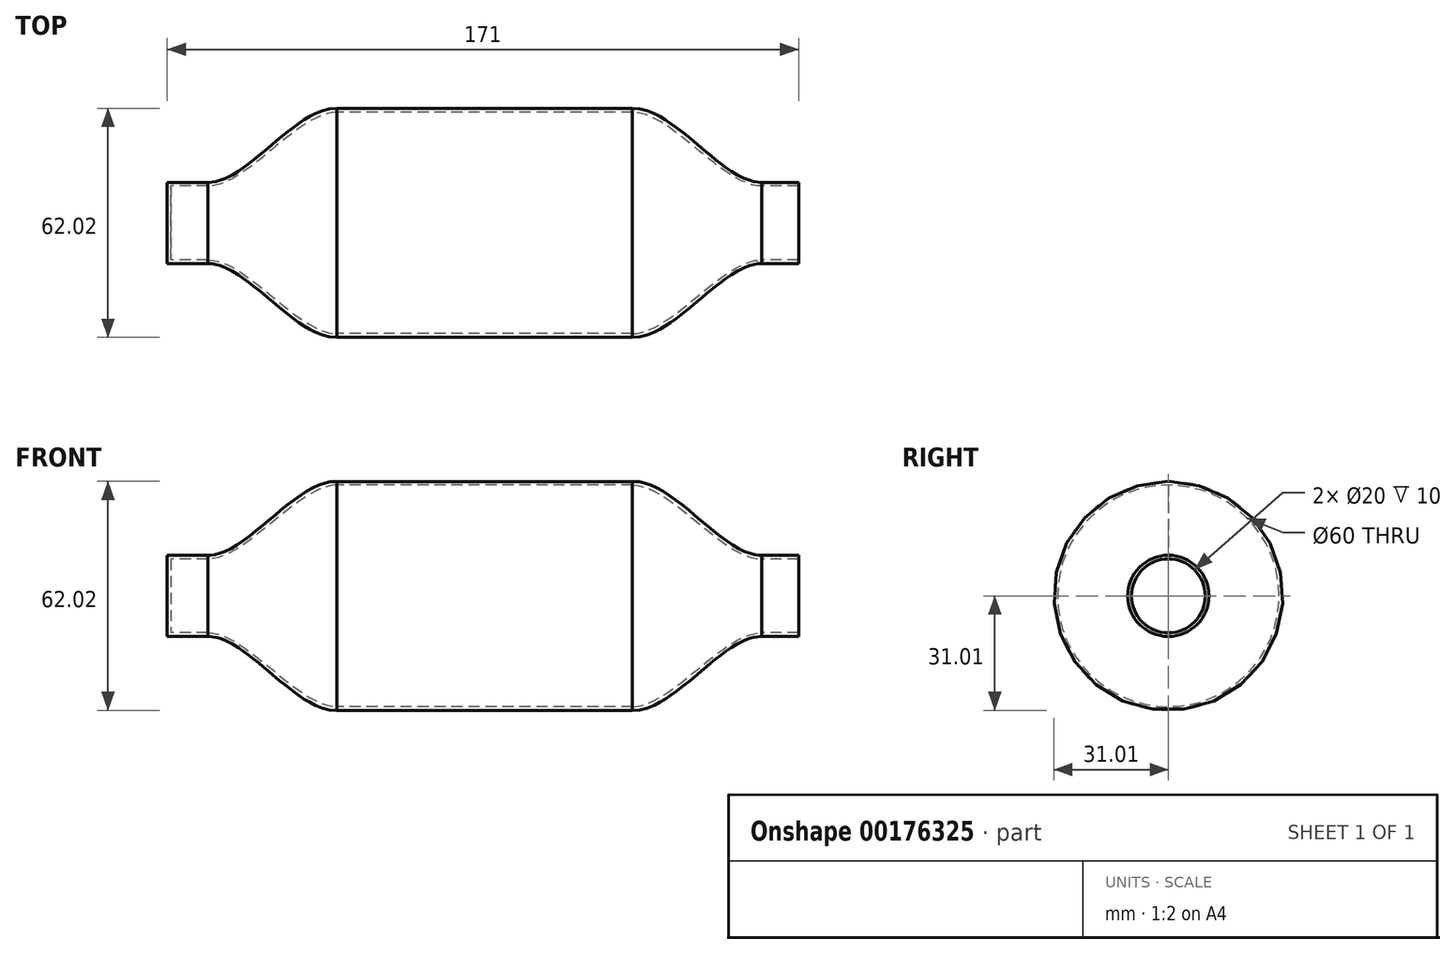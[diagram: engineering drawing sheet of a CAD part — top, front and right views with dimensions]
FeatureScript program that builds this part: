
annotation { "Feature Type Name" : "Feature", "Feature Type Description" : "" }
export const myFeature = defineFeature(function(context is Context, id is Id, definition is map)
    precondition{}
    {
        {
            var Q0;
            Q0=qCreatedBy(makeId("Top.planeOp"),FACE);
            var sketch = newSketch(context, id + "F0", { "sketchPlane" : qUnion([Q0])});
            skLineSegment(sketch, "E0", {"start": v(-46.54, 10) * mm, "end": v(-36.54, 10) * mm});
            skLineSegment(sketch, "E1", {"start": v(123.46, 10) * mm, "end": v(113.46, 10) * mm});
            skLineSegment(sketch, "E2", {"start": v(-113.84, 0) * mm, "end": v(145.76, 0) * mm});
            skLineSegment(sketch, "E3", {"start": v(-1.54, 30) * mm, "end": v(78.46, 30) * mm});
            skFitSpline(sketch, "E4", {"points": [v(78.46, 30) * mm, v(113.46, 10) * mm], "startDerivative": vector(32.02, 0) * mm, "endDerivative": vector(32.02, 0) * mm});
            skFitSpline(sketch, "E5", {"points": [v(-1.54, 30) * mm, v(-36.54, 10) * mm], "startDerivative": vector(-32.02, 0) * mm, "endDerivative": vector(-32.02, 0) * mm});
            skLineSegment(sketch, "E6.0", {"start": v(123.46, 11) * mm, "end": v(113.46, 11) * mm});
            skLineSegment(sketch, "E6.1", {"start": v(-46.54, 11) * mm, "end": v(-36.54, 11) * mm});
            skFitSpline(sketch, "E6.2", {"points": [v(-1.54, 31) * mm, v(-2.28, 31) * mm, v(-3.78, 30.83) * mm, v(-6.78, 29.9) * mm, v(-10.54, 27.87) * mm, v(-15.1, 24.53) * mm, v(-19.68, 20.77) * mm, v(-24.22, 17.03) * mm, v(-28.64, 13.8) * mm, v(-32.14, 11.93) * mm, v(-34.73, 11.14) * mm, v(-35.95, 11) * mm, v(-36.54, 11) * mm]});
            skLineSegment(sketch, "E6.3", {"start": v(-1.54, 31) * mm, "end": v(78.46, 31) * mm});
            skFitSpline(sketch, "E6.4", {"points": [v(78.46, 31) * mm, v(79.2, 31) * mm, v(80.7, 30.83) * mm, v(83.7, 29.9) * mm, v(87.46, 27.87) * mm, v(92.02, 24.53) * mm, v(96.6, 20.77) * mm, v(101.14, 17.03) * mm, v(105.57, 13.8) * mm, v(109.06, 11.93) * mm, v(111.65, 11.14) * mm, v(112.87, 11) * mm, v(113.46, 11) * mm]});
            skLineSegment(sketch, "E7", {"start": v(-46.54, 10) * mm, "end": v(-46.54, 11) * mm});
            skLineSegment(sketch, "E8", {"start": v(123.46, 10) * mm, "end": v(123.46, 11) * mm});
            skSolve(sketch);
        }
        {
            var Q0;
            Q0=makeQuery(id+"F0.imprint","IMPRINT",FACE,{"disambiguationData":[TD([[makeQuery(id+"F0.imprint","IMPRINT",EDGE,{"derivedFrom":sQuery(id+"F0.wireOp",EDGE,"E0")}),1.0]])]});
            var Q1;
            Q1=sQuery(id+"F0.wireOp",EDGE,"E2");
            revolve(context, id + "F1", {"entities" : qUnion([Q0]), "axis" : qUnion([Q1]), "revolveType" : RevolveType.FULL});
        }
        {
            var Q0;
            Q0=sQuery(id+"F0.wireOp",VERTEX,"E7.start");
            var Q1;
            Q1=qCreatedBy(makeId("Right.planeOp"),FACE);
            cPlane(context, id + "F2", {"entities" : qUnion([Q0, Q1]), "cplaneType" : CPlaneType.PLANE_POINT, "offset" : 25 * mm, "width" : 150 * mm, "height" : 150 * mm});
        }
        {
            var Q0;
            Q0=qCreatedBy(id+"F2.planeOp",FACE);
            var sketch = newSketch(context, id + "F3", { "sketchPlane" : qUnion([Q0])});
            skCircle(sketch, "E9", {"center": v(0, 0) * mm, "radius": 11 * mm});
            skSolve(sketch);
        }
        {
            var Q0;
            Q0=makeQuery(id+"F3.imprint","IMPRINT",FACE,{"disambiguationData":[TD([[makeQuery(id+"F3.imprint","IMPRINT",EDGE,{"derivedFrom":sQuery(id+"F3.wireOp",EDGE,"E9")}),1.0]])]});
            extrude(context, id + "F4", {"entities" : qUnion([Q0]), "operationType" : NewBodyOperationType.ADD, "oppositeDirection" : true, "depth" : 1 * mm});
        }
    });
